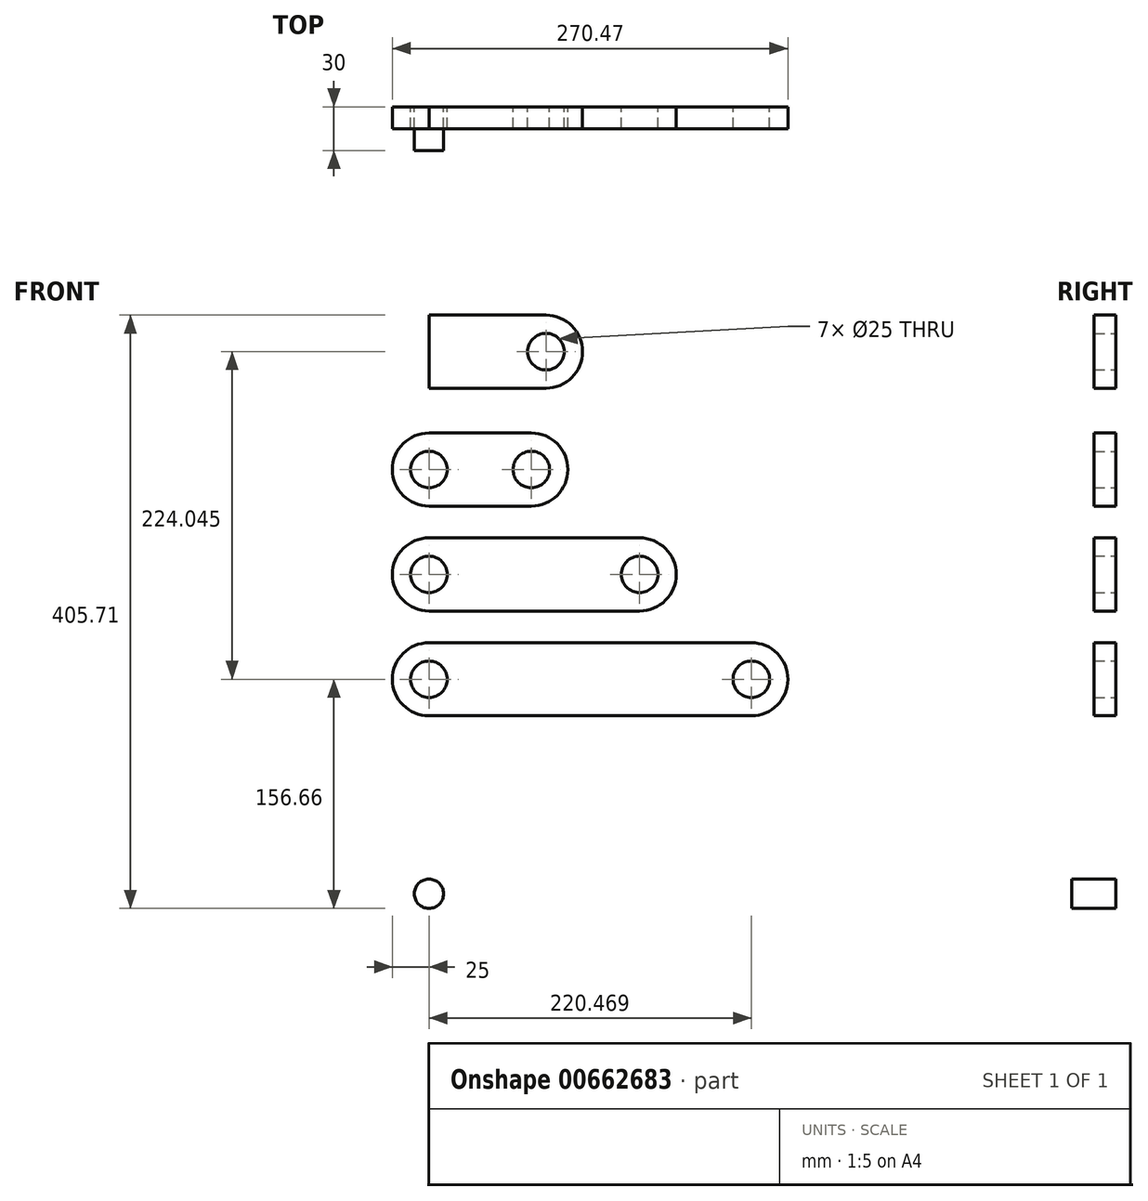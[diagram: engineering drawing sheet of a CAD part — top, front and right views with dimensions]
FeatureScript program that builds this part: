
annotation { "Feature Type Name" : "Feature", "Feature Type Description" : "" }
export const myFeature = defineFeature(function(context is Context, id is Id, definition is map)
    precondition{}
    {
        {
            var Q0;
            Q0=qCreatedBy(makeId("Front.planeOp"),FACE);
            var sketch = newSketch(context, id + "F0", { "sketchPlane" : qUnion([Q0])});
            skArc(sketch, "E0", {"start": v(0, 25) * mm, "mid": v(-25, 0) * mm, "end": v(0, -25) * mm});
            skArc(sketch, "E1", {"start": v(70, -25) * mm, "mid": v(95, 0) * mm, "end": v(70, 25) * mm});
            skLineSegment(sketch, "E2", {"start": v(0, 25) * mm, "end": v(70, 25) * mm});
            skLineSegment(sketch, "E3", {"start": v(0, -25) * mm, "end": v(70, -25) * mm});
            skCircle(sketch, "E4", {"center": v(0, 0) * mm, "radius": 12.5 * mm});
            skCircle(sketch, "E5", {"center": v(70, 0) * mm, "radius": 12.5 * mm});
            skSolve(sketch);
        }
        {
            var Q0;
            Q0=makeQuery(id+"F0.imprint","IMPRINT",FACE,{"disambiguationData":[TD([[makeQuery(id+"F0.imprint","IMPRINT",EDGE,{"derivedFrom":sQuery(id+"F0.wireOp",EDGE,"E0")}),1.0]])]});
            extrude(context, id + "F1", {"entities" : qUnion([Q0]), "depth" : 15 * mm, "offsetDistance" : 25 * mm});
        }
        {
            var Q0;
            Q0=qCreatedBy(makeId("Front.planeOp"),FACE);
            var sketch = newSketch(context, id + "F2", { "sketchPlane" : qUnion([Q0])});
            skLineSegment(sketch, "E6", {"start": v(0, 105.59) * mm, "end": v(0, 55.59) * mm});
            skLineSegment(sketch, "E7", {"start": v(0, 55.59) * mm, "end": v(80, 55.59) * mm});
            skLineSegment(sketch, "E8", {"start": v(80, 105.59) * mm, "end": v(0, 105.59) * mm});
            skArc(sketch, "E9", {"start": v(80, 55.59) * mm, "mid": v(105, 80.59) * mm, "end": v(80, 105.59) * mm});
            skCircle(sketch, "E10", {"center": v(80, 80.59) * mm, "radius": 12.5 * mm});
            skSolve(sketch);
        }
        {
            var Q0;
            Q0=makeQuery(id+"F2.imprint","IMPRINT",FACE,{"disambiguationData":[TD([[makeQuery(id+"F2.imprint","IMPRINT",EDGE,{"derivedFrom":sQuery(id+"F2.wireOp",EDGE,"E6")}),1.0]])]});
            extrude(context, id + "F3", {"entities" : qUnion([Q0]), "depth" : 15 * mm, "offsetDistance" : 25 * mm});
        }
        {
            var Q0;
            Q0=qCreatedBy(makeId("Front.planeOp"),FACE);
            var sketch = newSketch(context, id + "F4", { "sketchPlane" : qUnion([Q0])});
            skCircle(sketch, "E11", {"center": v(0, -71.74) * mm, "radius": 12.5 * mm});
            skArc(sketch, "E12", {"start": v(0, -46.74) * mm, "mid": v(-25, -71.74) * mm, "end": v(0, -96.74) * mm});
            skLineSegment(sketch, "E13", {"start": v(0, -46.74) * mm, "end": v(72.04, -46.74) * mm});
            skLineSegment(sketch, "E14", {"start": v(72.04, -30.13) * mm, "end": v(72.04, -114.82) * mm, "construction": true});
            skLineSegment(sketch, "E15", {"start": v(0, -96.74) * mm, "end": v(72.04, -96.74) * mm});
            skCircle(sketch, "E16.MirrorC", {"center": v(144.09, -71.74) * mm, "radius": 12.5 * mm});
            skArc(sketch, "E17.MirrorC", {"start": v(144.09, -46.74) * mm, "mid": v(169.09, -71.74) * mm, "end": v(144.09, -96.74) * mm});
            skLineSegment(sketch, "E18.MirrorCS", {"start": v(144.09, -96.74) * mm, "end": v(72.04, -96.74) * mm});
            skLineSegment(sketch, "E19.MirrorCS", {"start": v(144.09, -46.74) * mm, "end": v(72.04, -46.74) * mm});
            skSolve(sketch);
        }
        {
            var Q0;
            Q0 = qSketchRegion(id + "F4", true);
            extrude(context, id + "F5", {"entities" : qUnion([Q0]), "depth" : 15 * mm, "offsetDistance" : 25 * mm});
        }
        {
            var Q0;
            Q0=qCreatedBy(makeId("Front.planeOp"),FACE);
            var sketch = newSketch(context, id + "F6", { "sketchPlane" : qUnion([Q0])});
            skCircle(sketch, "E20", {"center": v(0, -143.46) * mm, "radius": 12.5 * mm});
            skArc(sketch, "E21", {"start": v(0, -118.46) * mm, "mid": v(-25, -143.46) * mm, "end": v(0, -168.46) * mm});
            skLineSegment(sketch, "E22", {"start": v(0, -118.46) * mm, "end": v(110.23, -118.46) * mm});
            skLineSegment(sketch, "E23", {"start": v(0, -168.46) * mm, "end": v(110.23, -168.46) * mm});
            skLineSegment(sketch, "E24", {"start": v(110.23, -103.6) * mm, "end": v(110.23, -180.4) * mm, "construction": true});
            skLineSegment(sketch, "E25.MirrorCS", {"start": v(220.47, -168.46) * mm, "end": v(110.23, -168.46) * mm});
            skLineSegment(sketch, "E26.MirrorCS", {"start": v(220.47, -118.46) * mm, "end": v(110.23, -118.46) * mm});
            skCircle(sketch, "E27.MirrorC", {"center": v(220.47, -143.46) * mm, "radius": 12.5 * mm});
            skArc(sketch, "E28.MirrorC", {"start": v(220.47, -118.46) * mm, "mid": v(245.47, -143.46) * mm, "end": v(220.47, -168.46) * mm});
            skSolve(sketch);
        }
        {
            var Q0;
            Q0 = qSketchRegion(id + "F6", true);
            extrude(context, id + "F7", {"entities" : qUnion([Q0]), "depth" : 15 * mm, "offsetDistance" : 25 * mm});
        }
        {
            var Q0;
            Q0=qCreatedBy(makeId("Front.planeOp"),FACE);
            var sketch = newSketch(context, id + "F8", { "sketchPlane" : qUnion([Q0])});
            skCircle(sketch, "E29", {"center": v(0, -290.12) * mm, "radius": 10 * mm});
            skSolve(sketch);
        }
        {
            var Q0;
            Q0 = qSketchRegion(id + "F8", true);
            extrude(context, id + "F9", {"entities" : qUnion([Q0]), "depth" : 30 * mm, "offsetDistance" : 25 * mm});
        }
    });
